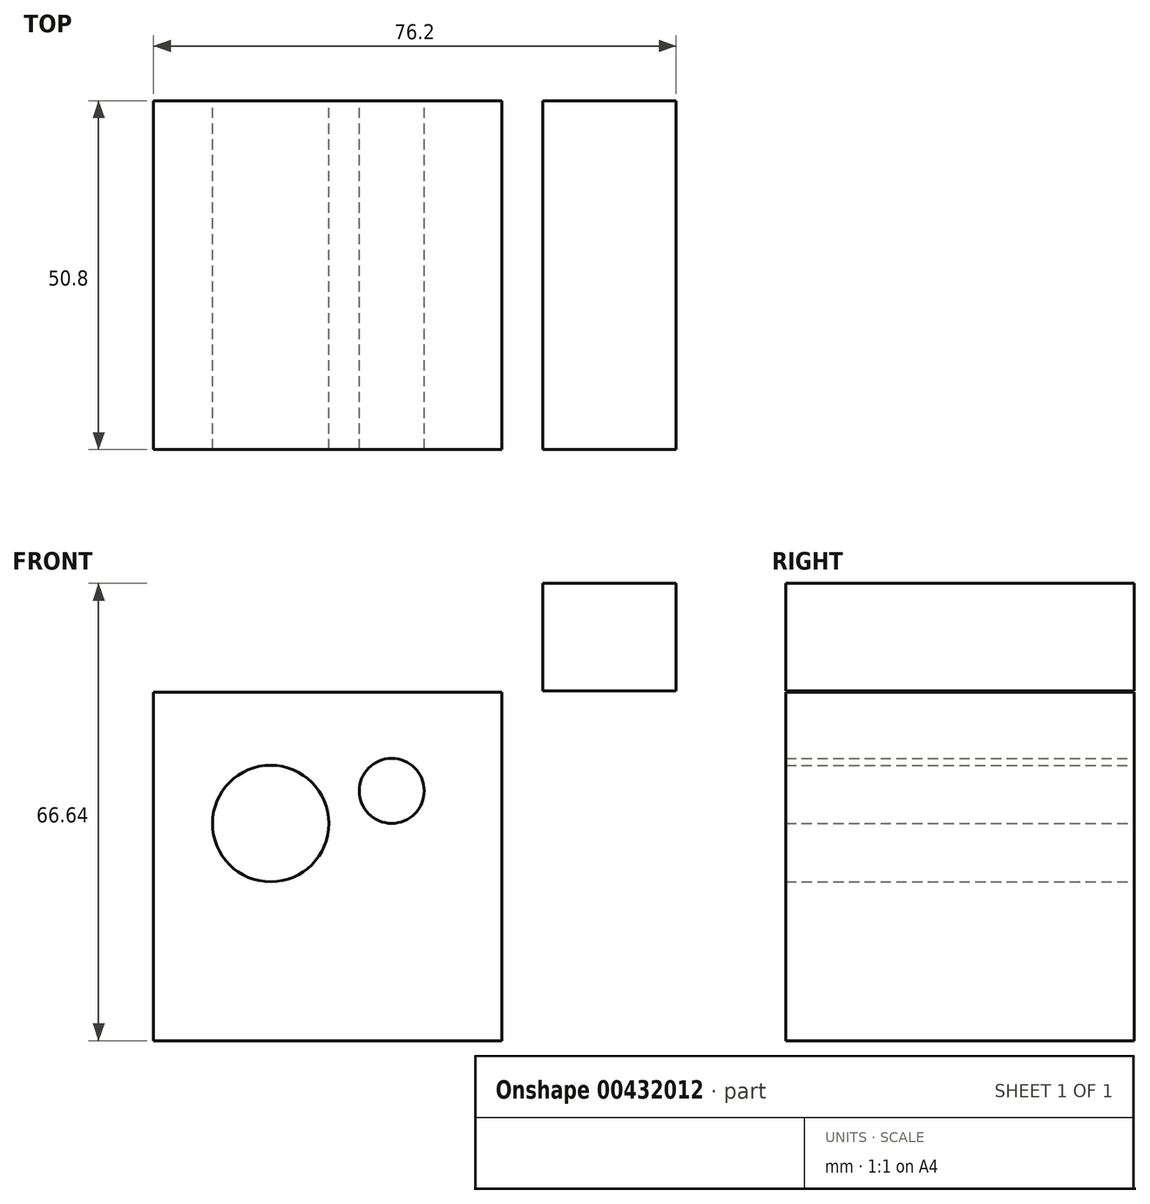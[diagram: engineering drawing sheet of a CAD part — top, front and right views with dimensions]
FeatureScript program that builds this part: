
annotation { "Feature Type Name" : "Feature", "Feature Type Description" : "" }
export const myFeature = defineFeature(function(context is Context, id is Id, definition is map)
    precondition{}
    {
        {
            var Q0;
            Q0=qCreatedBy(makeId("Front.planeOp"),FACE);
            var sketch = newSketch(context, id + "F0", { "sketchPlane" : qUnion([Q0])});
            skLineSegment(sketch, "E0.bottom", {"start": v(-19.26, 35.92) * mm, "end": v(31.54, 35.92) * mm});
            skLineSegment(sketch, "E0.top", {"start": v(-19.26, -14.88) * mm, "end": v(31.54, -14.88) * mm});
            skLineSegment(sketch, "E0.left", {"start": v(-19.26, 35.92) * mm, "end": v(-19.26, -14.88) * mm});
            skLineSegment(sketch, "E0.right", {"start": v(31.54, 35.92) * mm, "end": v(31.54, -14.88) * mm});
            skLineSegment(sketch, "E1.bottom", {"start": v(37.5, 51.76) * mm, "end": v(56.94, 51.76) * mm});
            skLineSegment(sketch, "E1.top", {"start": v(37.5, 36.08) * mm, "end": v(56.94, 36.08) * mm});
            skLineSegment(sketch, "E1.left", {"start": v(37.5, 51.76) * mm, "end": v(37.5, 36.08) * mm});
            skLineSegment(sketch, "E1.right", {"start": v(56.94, 51.76) * mm, "end": v(56.94, 36.08) * mm});
            skCircle(sketch, "E2", {"center": v(15.47, 21.51) * mm, "radius": 4.73 * mm});
            skCircle(sketch, "E3", {"center": v(-2.18, 16.76) * mm, "radius": 8.49 * mm});
            skSolve(sketch);
        }
        {
            var Q0;
            Q0=makeQuery(id+"F0.imprint","IMPRINT",FACE,{"disambiguationData":[TD([[makeQuery(id+"F0.imprint","IMPRINT",EDGE,{"derivedFrom":sQuery(id+"F0.wireOp",EDGE,"E1.bottom")}),-1.0]])]});
            var Q1;
            Q1=makeQuery(id+"F0.imprint","IMPRINT",FACE,{"disambiguationData":[TD([[makeQuery(id+"F0.imprint","IMPRINT",EDGE,{"derivedFrom":sQuery(id+"F0.wireOp",EDGE,"E0.bottom")}),-1.0]])]});
            extrude(context, id + "F1", {"entities" : qUnion([Q0, Q1]), "depth" : 50.8 * mm});
        }
    });
